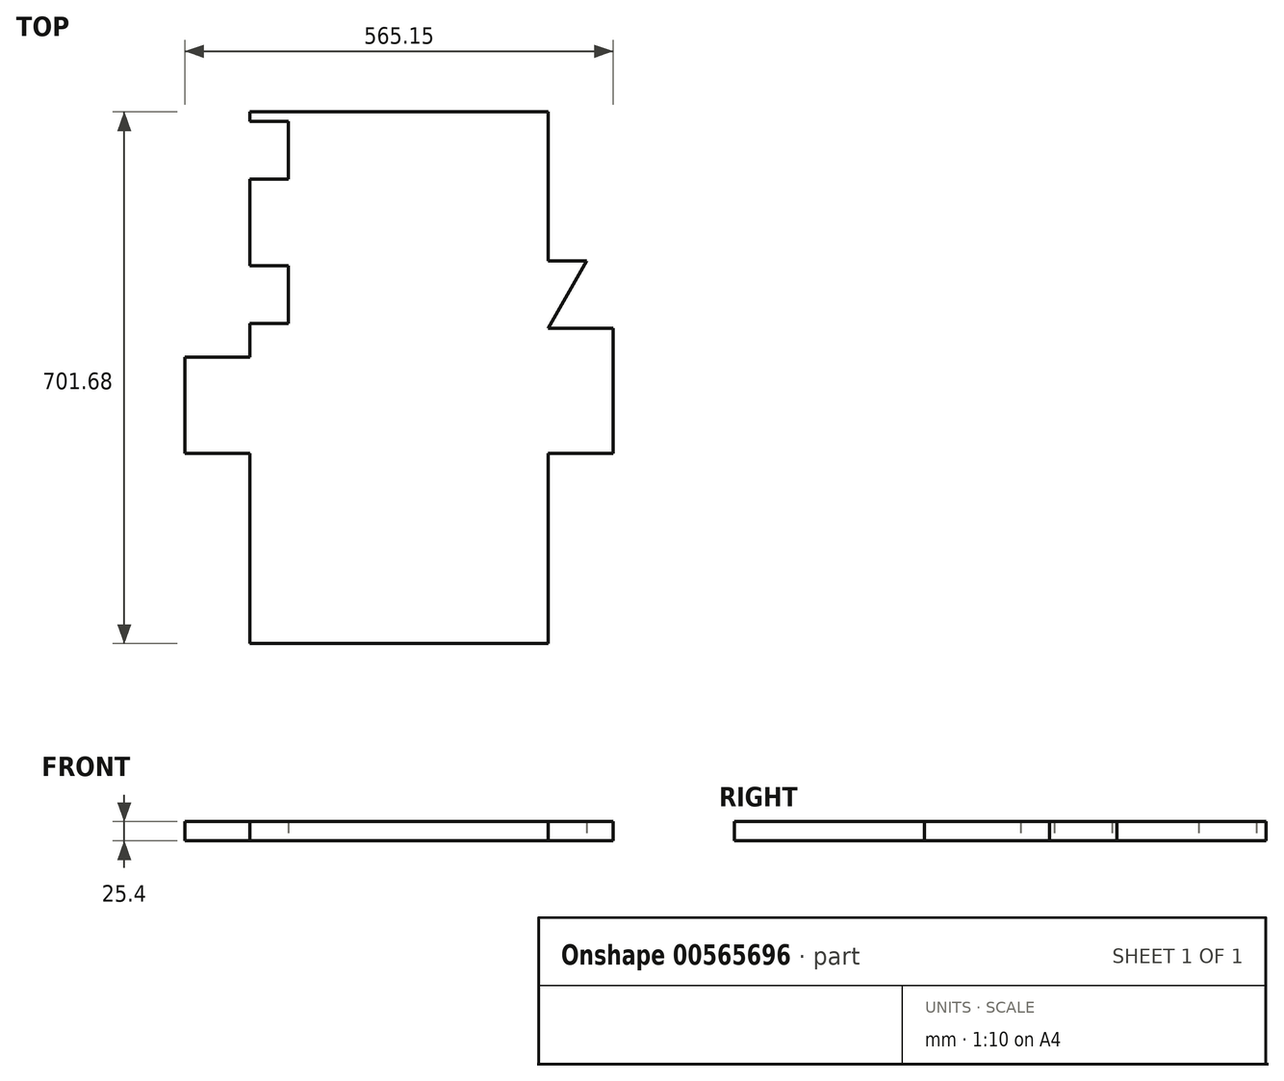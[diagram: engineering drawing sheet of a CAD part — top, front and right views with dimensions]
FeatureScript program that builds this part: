
annotation { "Feature Type Name" : "Feature", "Feature Type Description" : "" }
export const myFeature = defineFeature(function(context is Context, id is Id, definition is map)
    precondition{}
    {
        {
            var Q0;
            Q0=qCreatedBy(makeId("Top.planeOp"),FACE);
            var sketch = newSketch(context, id + "F0", { "sketchPlane" : qUnion([Q0])});
            skLineSegment(sketch, "E0", {"start": v(0, 0) * mm, "end": v(393.7, 0) * mm});
            skLineSegment(sketch, "E1", {"start": v(393.7, 0) * mm, "end": v(393.7, 250.83) * mm});
            skLineSegment(sketch, "E2", {"start": v(393.7, 250.83) * mm, "end": v(479.43, 250.83) * mm});
            skLineSegment(sketch, "E3", {"start": v(479.43, 250.83) * mm, "end": v(479.43, 415.93) * mm});
            skLineSegment(sketch, "E4", {"start": v(479.43, 415.93) * mm, "end": v(393.7, 415.93) * mm});
            skLineSegment(sketch, "E5", {"start": v(393.7, 415.93) * mm, "end": v(393.7, 504.83) * mm});
            skLineSegment(sketch, "E6", {"start": v(393.7, 504.83) * mm, "end": v(393.7, 701.68) * mm});
            skLineSegment(sketch, "E7", {"start": v(393.7, 701.68) * mm, "end": v(0, 701.68) * mm});
            skLineSegment(sketch, "E8", {"start": v(0, 701.68) * mm, "end": v(0, 688.98) * mm});
            skLineSegment(sketch, "E9", {"start": v(0, 688.98) * mm, "end": v(50.8, 688.98) * mm});
            skLineSegment(sketch, "E10", {"start": v(50.8, 688.98) * mm, "end": v(50.8, 612.77) * mm});
            skLineSegment(sketch, "E11", {"start": v(50.8, 612.77) * mm, "end": v(0, 612.77) * mm});
            skLineSegment(sketch, "E12", {"start": v(0, 612.77) * mm, "end": v(0, 498.47) * mm});
            skLineSegment(sketch, "E13", {"start": v(0, 498.47) * mm, "end": v(50.8, 498.47) * mm});
            skLineSegment(sketch, "E14", {"start": v(50.8, 498.47) * mm, "end": v(50.8, 422.27) * mm});
            skLineSegment(sketch, "E15", {"start": v(50.8, 422.27) * mm, "end": v(0, 422.27) * mm});
            skLineSegment(sketch, "E16", {"start": v(0, 422.27) * mm, "end": v(0, 377.82) * mm});
            skLineSegment(sketch, "E17", {"start": v(0, 377.82) * mm, "end": v(-85.72, 377.82) * mm});
            skLineSegment(sketch, "E18", {"start": v(-85.72, 377.82) * mm, "end": v(-85.72, 250.83) * mm});
            skLineSegment(sketch, "E19", {"start": v(-85.72, 250.83) * mm, "end": v(0, 250.83) * mm});
            skLineSegment(sketch, "E20", {"start": v(0, 250.83) * mm, "end": v(0, 0) * mm});
            skLineSegment(sketch, "E21", {"start": v(393.7, 504.83) * mm, "end": v(444.5, 504.83) * mm});
            skLineSegment(sketch, "E22", {"start": v(444.5, 504.83) * mm, "end": v(393.7, 415.93) * mm});
            skSolve(sketch);
        }
        {
            var Q0;
            Q0 = qSketchRegion(id + "F0", true);
            extrude(context, id + "F1", {"entities" : qUnion([Q0]), "depth" : 25.4 * mm, "offsetDistance" : 25.4 * mm});
        }
    });
